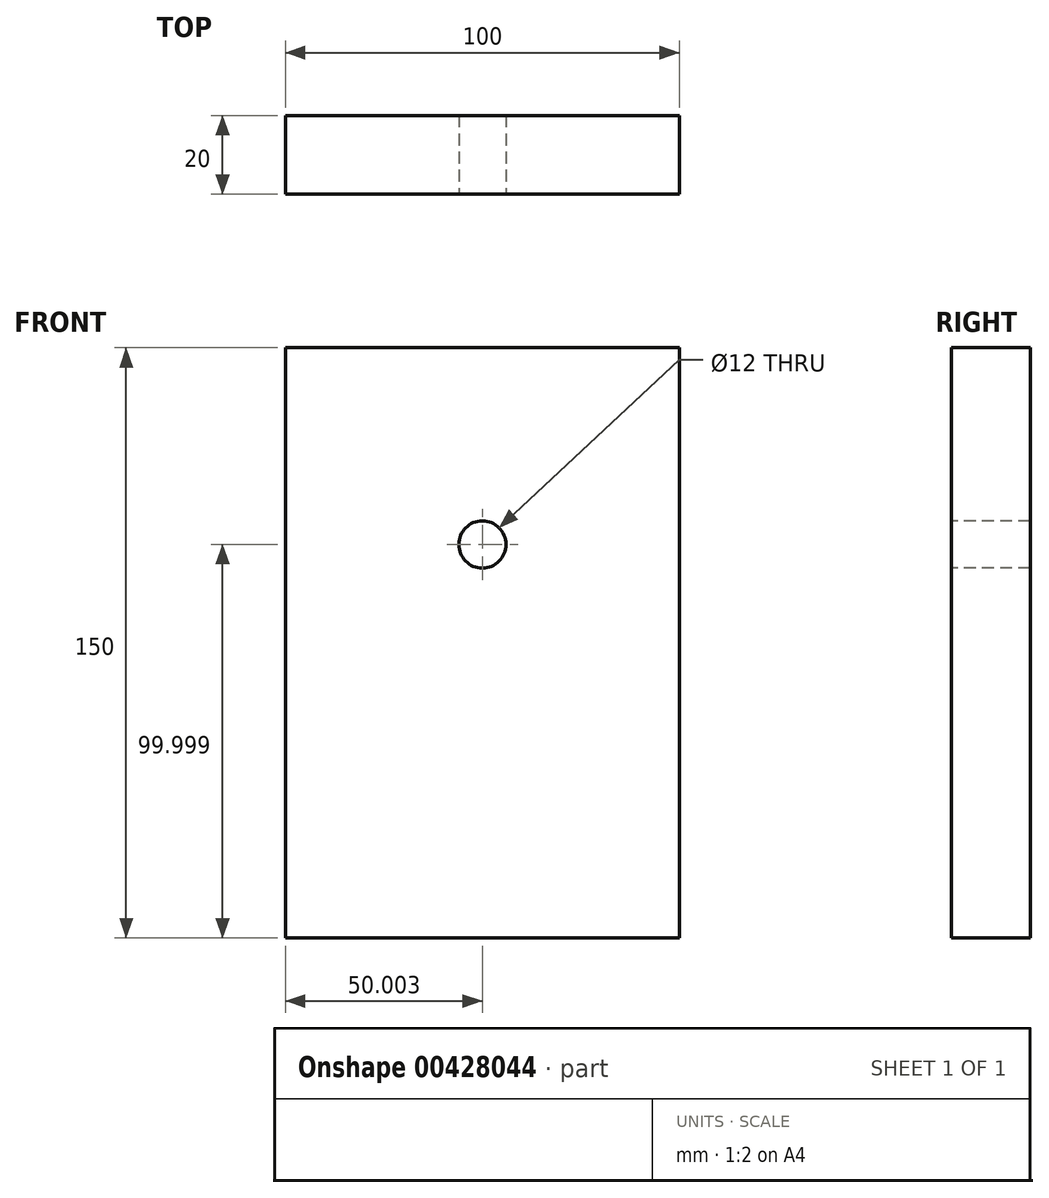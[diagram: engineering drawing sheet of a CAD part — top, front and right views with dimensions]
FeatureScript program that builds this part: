
annotation { "Feature Type Name" : "Feature", "Feature Type Description" : "" }
export const myFeature = defineFeature(function(context is Context, id is Id, definition is map)
    precondition{}
    {
        {
            var Q0;
            Q0=qCreatedBy(makeId("Front.planeOp"),FACE);
            var sketch = newSketch(context, id + "F0", { "sketchPlane" : qUnion([Q0])});
            skLineSegment(sketch, "E0.bottom", {"start": v(-50.98, 83.3) * mm, "end": v(49.02, 83.3) * mm});
            skLineSegment(sketch, "E0.top", {"start": v(-50.98, -66.7) * mm, "end": v(49.02, -66.7) * mm});
            skLineSegment(sketch, "E0.left", {"start": v(-50.98, 83.3) * mm, "end": v(-50.98, -66.7) * mm});
            skLineSegment(sketch, "E0.right", {"start": v(49.02, 83.3) * mm, "end": v(49.02, -66.7) * mm});
            skSolve(sketch);
        }
        {
            var Q0;
            Q0 = qSketchRegion(id + "F0", true);
            extrude(context, id + "F1", {"entities" : qUnion([Q0]), "depth" : 20 * mm});
        }
        {
            var Q0;
            Q0=makeQuery(id+"F1.opExtrude","CAP_FACE",FACE,{"disambiguationData":[OSD([sQuery(id+"F0.wireOp",EDGE,"E0.bottom"),sQuery(id+"F0.wireOp",EDGE,"E0.top"),sQuery(id+"F0.wireOp",EDGE,"E0.left"),sQuery(id+"F0.wireOp",EDGE,"E0.right")])],"isStart":false});
            var sketch = newSketch(context, id + "F2", { "sketchPlane" : qUnion([Q0])});
            skLineSegment(sketch, "E1", {"start": v(-0.98, 83.3) * mm, "end": v(-0.98, 33.3) * mm});
            skCircle(sketch, "E2", {"center": v(-0.98, 33.3) * mm, "radius": 6 * mm});
            skSolve(sketch);
        }
        {
            var Q0;
            Q0 = qSketchRegion(id + "F2", true);
            extrude(context, id + "F3", {"entities" : qUnion([Q0]), "operationType" : NewBodyOperationType.REMOVE, "oppositeDirection" : true, "depth" : 25 * mm});
        }
    });
